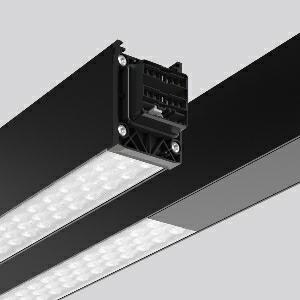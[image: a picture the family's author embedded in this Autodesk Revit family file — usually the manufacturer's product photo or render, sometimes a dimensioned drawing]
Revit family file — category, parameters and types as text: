
# Revit family: linedo_4_5m_30_11001100_954530_853_776_501_c769
name_source: partatom
category: Lighting Fixtures
units: mm (PartAtom-declared; Revit-internal decimal feet)

## family parameters
Cut with Voids When Loaded = No
Host = Face
Light Source = No
Part Type = Normal
Room Calculation Point = No
Round Connector Dimension = Use Diameter
Shared = No

## types (1)
- LINEDO_4,5m_30_11001100 (1 x LED Modul 850, 2487.5 lm, 5000)
    Apparent Load = 60 VA
    CIE Flux Codes = 89 97 99 100 100
    Color Rendering = 80
    Color Temperature = 5000
    Default Elevation = 1800 mm
    Description = LINEDO, 60 W, 9950 lm, 850, black, DALI
Continuous line luminaire, L 4547 B 58 H 76
    Height = 76 mm
    Lamp = 1 x LED Modul 850
    Lamp Light Flux = 2487.5 lm
    Lamp count = 1
    Length = 4547 mm
    Lifetime = 50000 h
    Luminous efficacy = 166 lm/W
    Manufacturer = RZB
    ModVariant = No
    Model = 954530.853.776.501
    Mounting Place = Ceiling
    Mounting Type = Surface mounted, Pendant
    Number of Poles = 1
    OnlyDefault = Yes
    Power Factor = 1
    Product Name = LINEDO_4,5m_30_11001100
    Product group = Surface mounted continuous line luminaire system
    ProductGroupID = 310
    Protection Class = Protection class I
    Protection Degree = IP 54
    RLX_Detail_Level = 1
    RLX_Emergency_Light_Flux = 0 lm
    RLX_Emergency_Type = 0
    RLX_Emergency_Type_DB = No
    RlxData = <blob elided: 56861 chars, md5=2fcb0d5a>
    Socket = socket
    Standby Power = 0 W
    System Light Flux = 9950 lm
    System Power = 60 W
    Type Comments = Product without accessories
    Type Image = 954530.853.476.504.jpg
    URL = http://relux.com
    VarID = ---
    Voltage = 230 V
    Voltage Range = 220-240 V
    Weight = 0.00 kg
    Width = 58 mm

## geometry (parser evidence)
native form markers: Blend x4, Sweep x20
no freeform markers — native parametric forms only
